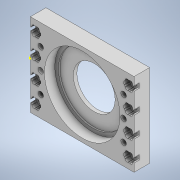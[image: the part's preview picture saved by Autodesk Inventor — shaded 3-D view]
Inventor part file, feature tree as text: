
AUTODESK INVENTOR PART (.ipt)
format: ipt  version: 2020 (Build 240168000, 168)  size: 435,712 bytes
history: native  units: in
note: dims shown in document units (in); Inventor stores cm internally (conversion verified against a paired STEP export)
features: sketch x9, extrude x8, fillet x2, pattern_linear x1
ambient origin geometry x8: Origin, YZ Plane, XZ Plane, XY Plane, X Axis, Y Axis, Z Axis, Center Point
bodies: Solid1 (feature_tree)
feature tree (20):
  extrude  "Extrusion1"  Depth=4.0in
  extrude  "Extrusion2"  Depth=5.0in
  extrude  "Extrusion3"  Depth=2.0in
  extrude  "Extrusion4"  Depth=3.3in
  extrude  "Extrusion5"  Depth=0.5787in
  extrude  "Extrusion6"  Depth=1.0in
  extrude  "Extrusion7"  Depth=0.5in
  fillet  "Fillet1"  Radius=0.25in
  pattern_linear  "Rectangular Pattern1"  Spacing1=0.25in  [1 undecoded]
  sketch  "Sketch9"  dims[d27=0.0in d28=0.0in]
  extrude  "Extrusion8"  Depth=0.0625in
  fillet  "Fillet2"  Radius=0.25in
  sketch  "Sketch1"  dims[d0=0.75in d1=4.0in]
  sketch  "Sketch2"  dims[d2=5.0in d3=0.0in d4=2.5in]
  sketch  "Sketch3"  dims[d5=2.0in d6=2.0157in]
  sketch  "Sketch5"  dims[d7=0.0in d8=0.0in d9=3.3in]
  sketch  "Sketch6"  dims[d10=0.5787in d11=0.0in d13=3.6407in]
  sketch  "Sketch7"  dims[d14=0.5in d15=0.0in d16=0.7874in d18=4.5in d19=1.5748in d21=1.0in]
  sketch  "Sketch8"  dims[d24=0.2656in d25=0.5in d26=0.25in]
  sketch  "Sketch10"  dims[d29=0.4532in d30=0.25in d31=0.0in d33=0.175in d34=0.25in d35=0.0in d36=0.0625in d37=1.5748in d39=1.0in d40=0.7874in d42=4.5in d43=2.0in d44=1.0in d45=1.1811in d47=1.0in d48=0.7874in d50=4.0in d53=0.0in d54=0.0in d55=0.0625in]
note: 1 required parameter value undecoded (feature->parameter linkage not recoverable at this tier; creation-order binding heuristic only, values carry confidence <= 0.55)
